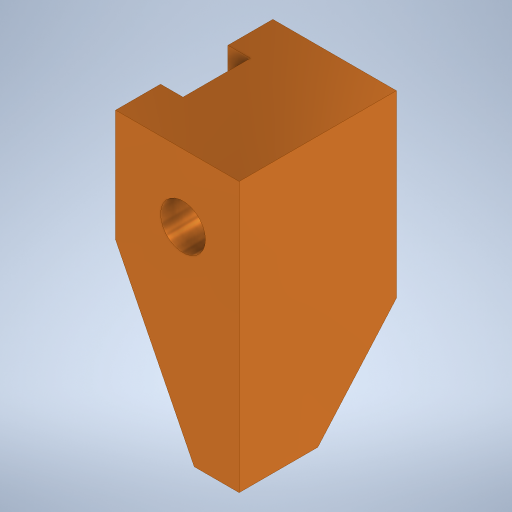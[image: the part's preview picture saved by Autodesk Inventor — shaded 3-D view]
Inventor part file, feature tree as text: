
AUTODESK INVENTOR PART (.ipt)
format: ipt  version: 2024 (Build 280153000, 153)  size: 235,520 bytes
history: native  units: in
note: dims shown in document units (in); Inventor stores cm internally (conversion verified against a paired STEP export)
features: chamfer x2, hole x2, extrude x1, other x1
ambient origin geometry x8: Origin, YZ Plane, XZ Plane, XY Plane, X Axis, Y Axis, Z Axis, Center Point
bodies: Solid1 (feature_tree)
feature tree (6):
  extrude  "NOTCHED SHAPE"  Depth=3.5in
  chamfer  "TOP SURF"  Distance=2.75in
  chamfer  "EDGE SURF"  Distance=0.5in
  hole  "HOLE CUTOUT"  [1 undecoded]
  other  "CONSTRAINED RECTS"
  hole  "HOLE"  [1 undecoded]
note: 2 required parameter values undecoded (feature->parameter linkage not recoverable at this tier; creation-order binding heuristic only, values carry confidence <= 0.55)
